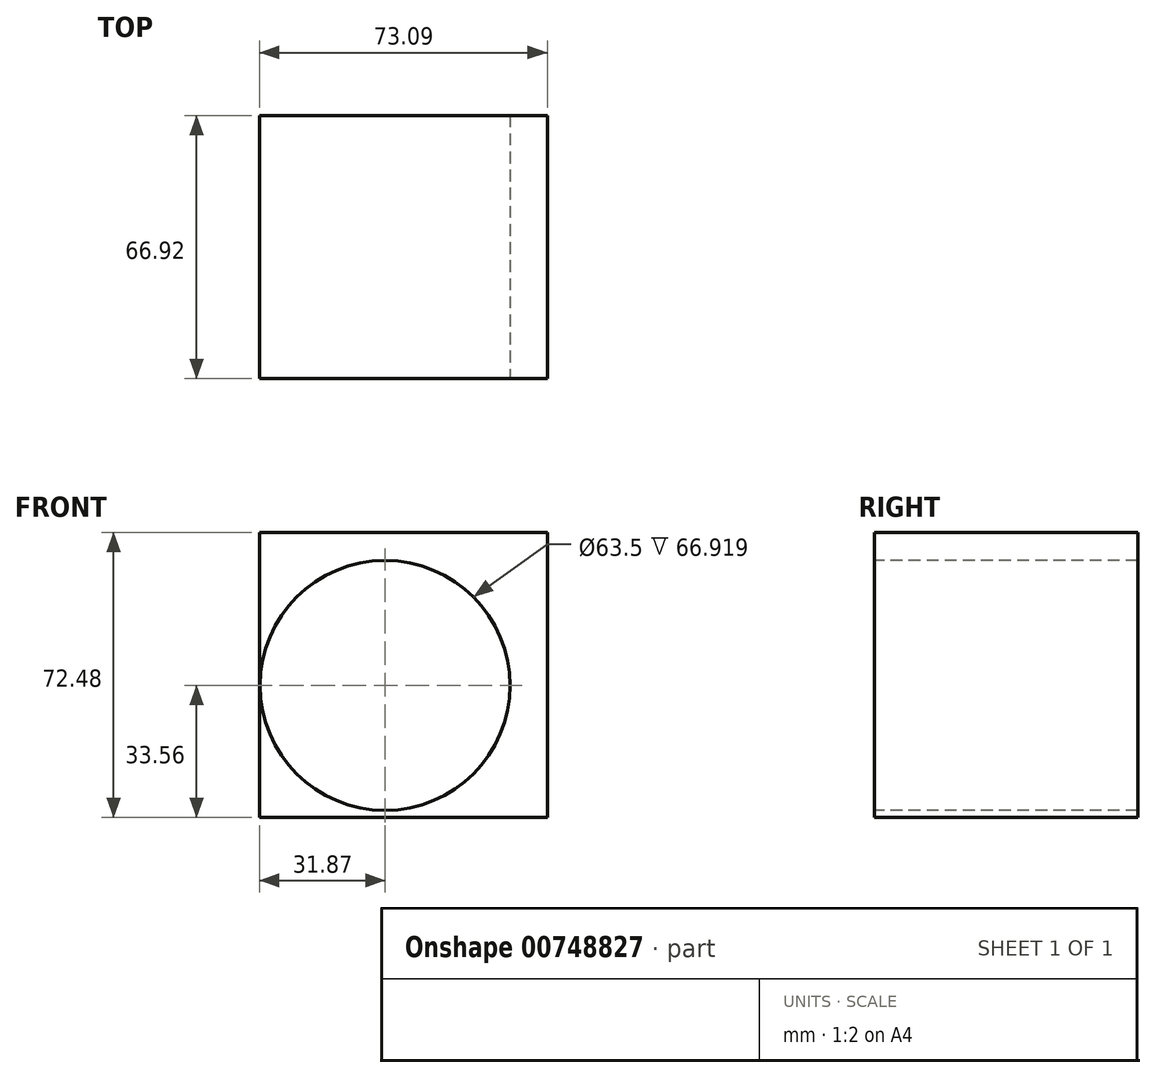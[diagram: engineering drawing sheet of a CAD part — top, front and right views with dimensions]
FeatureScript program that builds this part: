
annotation { "Feature Type Name" : "Feature", "Feature Type Description" : "" }
export const myFeature = defineFeature(function(context is Context, id is Id, definition is map)
    precondition{}
    {
        {
            var Q0;
            Q0=qCreatedBy(makeId("Front.planeOp"),FACE);
            var sketch = newSketch(context, id + "F0", { "sketchPlane" : qUnion([Q0])});
            skLineSegment(sketch, "E0.bottom", {"start": v(-31.87, -33.56) * mm, "end": v(41.22, -33.56) * mm});
            skLineSegment(sketch, "E0.top", {"start": v(-31.87, 38.92) * mm, "end": v(41.22, 38.92) * mm});
            skLineSegment(sketch, "E0.left", {"start": v(-31.87, -33.56) * mm, "end": v(-31.87, 38.92) * mm});
            skLineSegment(sketch, "E0.right", {"start": v(41.22, -33.56) * mm, "end": v(41.22, 38.92) * mm});
            skSolve(sketch);
        }
        {
            var Q0;
            Q0=makeQuery(id+"F0.imprint","IMPRINT",FACE,{"disambiguationData":[TD([[makeQuery(id+"F0.imprint","IMPRINT",EDGE,{"derivedFrom":sQuery(id+"F0.wireOp",EDGE,"E0.bottom")}),1.0]])]});
            extrude(context, id + "F1", {"entities" : qUnion([Q0]), "depth" : 66.92 * mm, "offsetDistance" : 25.4 * mm});
        }
        {
            var Q0;
            Q0=makeQuery(id+"F1.opExtrude","CAP_FACE",FACE,{"disambiguationData":[OSD([sQuery(id+"F0.wireOp",EDGE,"E0.bottom"),sQuery(id+"F0.wireOp",EDGE,"E0.top"),sQuery(id+"F0.wireOp",EDGE,"E0.left"),sQuery(id+"F0.wireOp",EDGE,"E0.right")])],"isStart":false});
            var sketch = newSketch(context, id + "F2", { "sketchPlane" : qUnion([Q0])});
            skPoint(sketch, "E1", {"position": v(0, 0) * mm});
            skSolve(sketch);
        }
        {
            var Q0;
            Q0=sQuery(id+"F2.wireOp",VERTEX,"E1");
            var Q1;
            Q1=makeQuery(id+"F1.opExtrude","SWEPT_BODY",BODY,{"disambiguationData":[OSD([sQuery(id+"F0.wireOp",EDGE,"E0.bottom"),sQuery(id+"F0.wireOp",EDGE,"E0.top"),sQuery(id+"F0.wireOp",EDGE,"E0.left"),sQuery(id+"F0.wireOp",EDGE,"E0.right")])]});
            hole(context, id + "F3", {"style" : HoleStyle.SIMPLE, "endStyle" : HoleEndStyle.THROUGH, "holeDiameter" : 63.5 * mm, "majorDiameter" : 6.35 * mm, "isTappedThrough" : true, "tappedDepth" : 12.7 * mm, "tapClearance" : 3, "locations" : qUnion([Q0]), "scope" : qUnion([Q1])});
        }
    });
